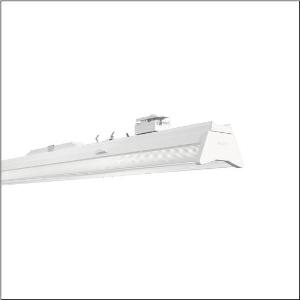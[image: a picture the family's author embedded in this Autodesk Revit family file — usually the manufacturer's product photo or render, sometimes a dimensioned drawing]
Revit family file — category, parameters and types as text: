
# Revit family: licross_r__21_performance_mo_52tm16dn445g3s_a020
name_source: partatom
category: Lighting Fixtures
units: mm (PartAtom-declared; Revit-internal decimal feet)

## family parameters
Cut with Voids When Loaded = No
Host = Face
Light Source = No
Part Type = Normal
Room Calculation Point = No
Round Connector Dimension = Use Diameter
Shared = No

## types (1)
- --- (1 x LED, 950 lm, 6.1 W, 4000K)
    Apparent Load = 6 VA
    CIE Flux Codes = 66 88 96 79 100
    Color Rendering = 80
    Color Temperature = 4000K
    Default Elevation = 1800 mm
    Description = Licross® 21 Performance MO, luminaire insert, of sheet steel, galvanised, coil coated, white, length: 1.500mm, width: 120mm, height: 123mm, LED rated luminous flux: 4.500lm, light colour: 840, SDCM (Standard Deviation of Colour Matching)MacAdam ≤ 3 SDCM (initial), control gear: DALI 2 (for two DALI lines), with plug, 6-pole, with phase selection, for trunking rail, 14-core, mains connection: 220..240V, AC, 50/60Hz, rated input power: 29W, for emergency light function, internal wiring halogen-free, for trunking rail, 14-core, converter,control gear: single battery element, battery: LiFePO4, 9Ah, primary light control with lens, of plastic, primary optical cover: cover, of PMMA, CAT 2 (L<= 3000cd/m²), light emission: direct/indirect distribution, primary light characteristic: symmetric, protection rating (complete): IP40, insulation class (complete): insulation class I (protective earthing), certification: CE, UKCA, protection symbol: D if used in an environment with non-conductive dust loads with corresponding accessories, impact resistance: IK06, permissible ambient temperature for indoor applications: -5..+35°C, standard: EN 60598-2-22, corresponds to IFS (International Featured Standards) requirements for safety and quality in the food industry, reducing of maximum allowable ambient temperature of 5°C with ceiling mounting, LABS conformity tested according to VDMA 24364:2018-05, packaging unit: 1 piece
    Height = 114 mm
    Lamp = 1 x LED
    Lamp Light Flux = 950 lm
    Lamp Power = 6.1 W
    Lamp count = 1
    Length = 1500 mm
    Luminous efficacy = 156 lm/W
    Manufacturer = Siteco
    ModVariant = No
    Model = 52TM16DN445G3S
    Mounting Place = Ceiling
    Mounting Type = Pendant
    Number of Poles = 1
    OnlyDefault = Yes
    Power Factor = 1
    Product Name = Licross® 21 Performance MO
    Product group = luminaire insert | ceiling pendant
    ProductGroupID = 901
    Protection Class = Protection class I
    Protection Degree = IP 40
    RLX_Detail_Level = 1
    RLX_Emergency_Light_Flux = 0 lm
    RLX_Emergency_Type = 0
    RLX_Emergency_Type_DB = No
    RlxData = <blob elided: 34089 chars, md5=7b70eba7>
    Socket = socket
    Standby Power = 0 W
    System Light Flux = 950 lm
    System Power = 6 W
    Type Comments = : emergency light operation: 3 h
    Type Image = l_1256138.jpg
    URL = http://relux.com
    VarID = @adj_040409
    Voltage = 0 V
    Weight = 0.00 kg
    Width = 120 mm

## geometry (parser evidence)
native form markers: Blend x4, Sweep x11
no freeform markers — native parametric forms only
